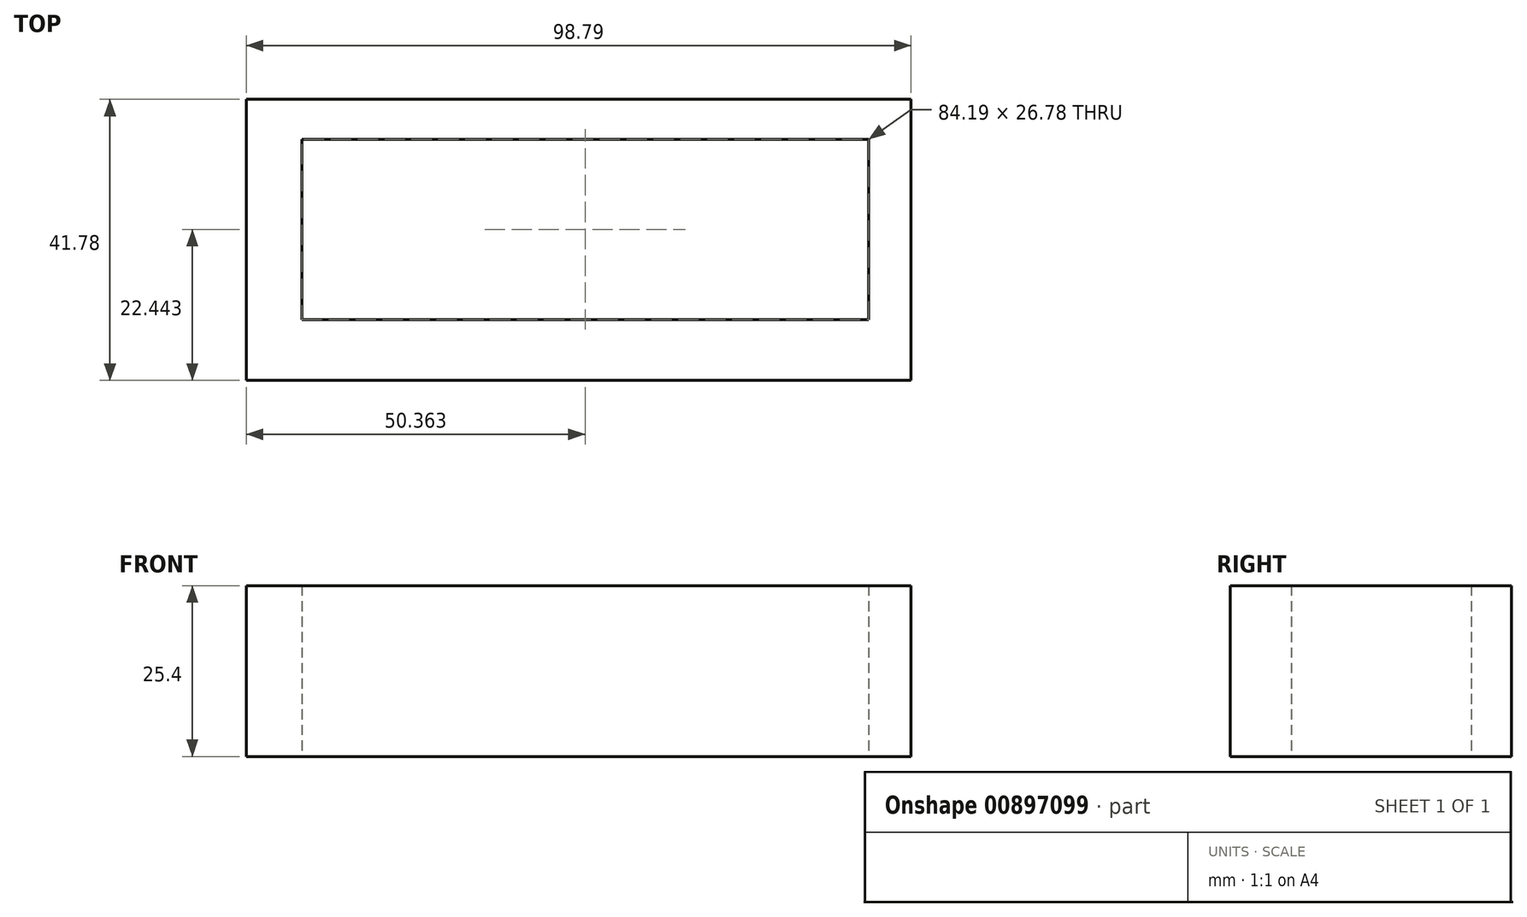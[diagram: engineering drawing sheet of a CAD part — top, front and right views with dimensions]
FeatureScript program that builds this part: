
annotation { "Feature Type Name" : "Feature", "Feature Type Description" : "" }
export const myFeature = defineFeature(function(context is Context, id is Id, definition is map)
    precondition{}
    {
        {
            var Q0;
            Q0=qCreatedBy(makeId("Top.planeOp"),FACE);
            var sketch = newSketch(context, id + "F0", { "sketchPlane" : qUnion([Q0])});
            skLineSegment(sketch, "E0.bottom", {"start": v(-31.1, 62) * mm, "end": v(-129.89, 62) * mm});
            skLineSegment(sketch, "E0.top", {"start": v(-31.1, 20.22) * mm, "end": v(-129.89, 20.22) * mm});
            skLineSegment(sketch, "E0.left", {"start": v(-31.1, 62) * mm, "end": v(-31.1, 20.22) * mm});
            skLineSegment(sketch, "E0.right", {"start": v(-129.89, 62) * mm, "end": v(-129.89, 20.22) * mm});
            skLineSegment(sketch, "E1.bottom", {"start": v(-37.43, 56.06) * mm, "end": v(-121.62, 56.06) * mm});
            skLineSegment(sketch, "E1.top", {"start": v(-37.43, 29.27) * mm, "end": v(-121.62, 29.27) * mm});
            skLineSegment(sketch, "E1.left", {"start": v(-37.43, 56.06) * mm, "end": v(-37.43, 29.27) * mm});
            skLineSegment(sketch, "E1.right", {"start": v(-121.62, 56.06) * mm, "end": v(-121.62, 29.27) * mm});
            skSolve(sketch);
        }
        {
            var Q0;
            Q0=makeQuery(id+"F0.imprint","IMPRINT",FACE,{"disambiguationData":[TD([[makeQuery(id+"F0.imprint","IMPRINT",EDGE,{"derivedFrom":sQuery(id+"F0.wireOp",EDGE,"E0.bottom")}),1.0]])]});
            extrude(context, id + "F1", {"entities" : qUnion([Q0]), "depth" : 25.4 * mm, "offsetDistance" : 25.4 * mm});
        }
    });
